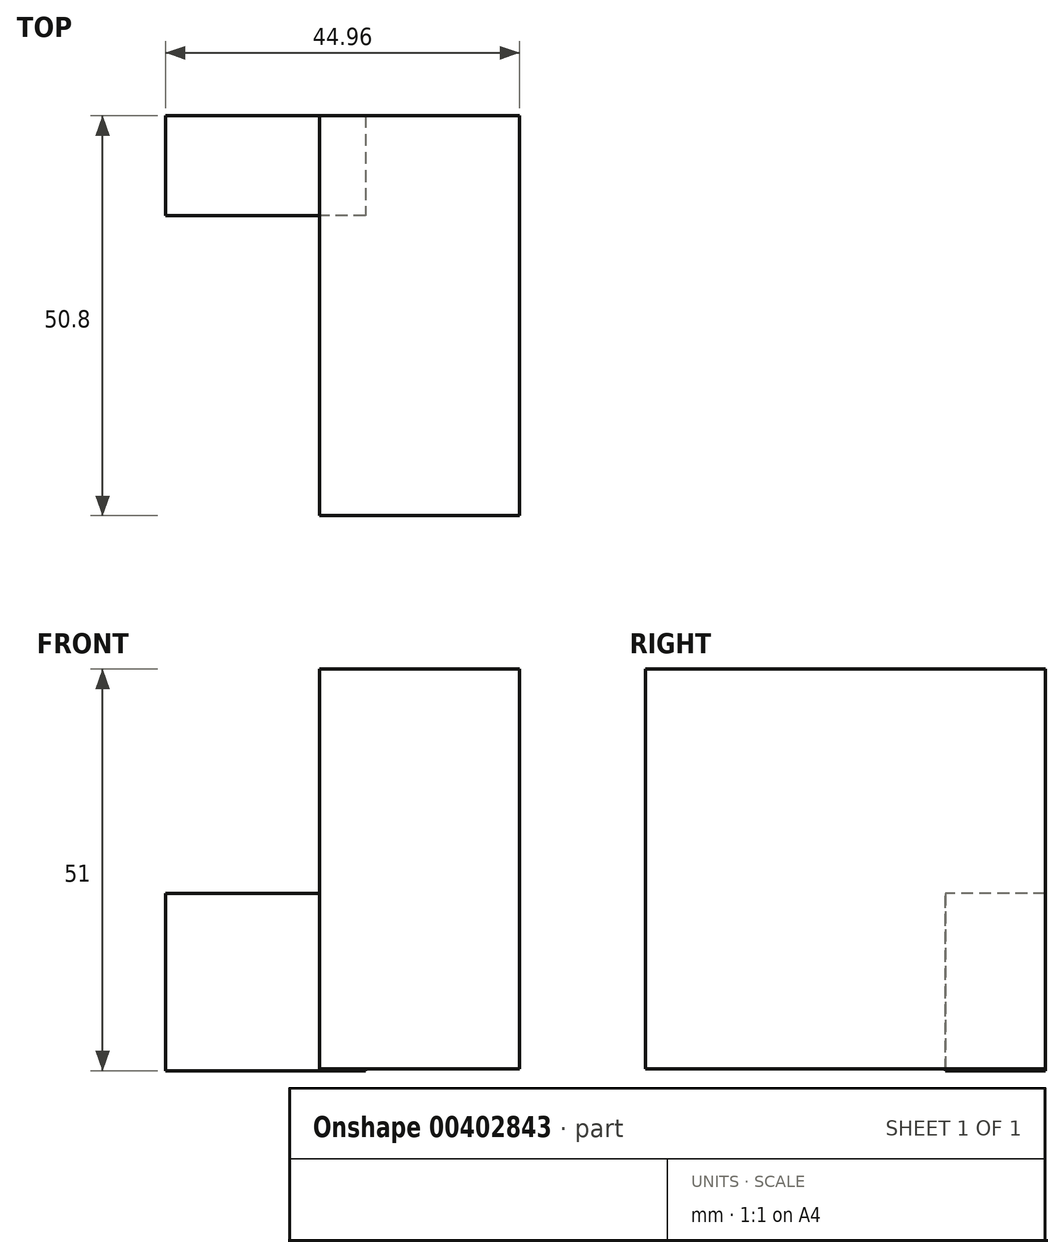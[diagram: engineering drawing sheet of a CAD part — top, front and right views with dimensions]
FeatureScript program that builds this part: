
annotation { "Feature Type Name" : "Feature", "Feature Type Description" : "" }
export const myFeature = defineFeature(function(context is Context, id is Id, definition is map)
    precondition{}
    {
        {
            var Q0;
            Q0=qCreatedBy(makeId("Front.planeOp"),FACE);
            var sketch = newSketch(context, id + "F0", { "sketchPlane" : qUnion([Q0])});
            skLineSegment(sketch, "E0", {"start": v(30.14, -31.41) * mm, "end": v(30.14, 19.39) * mm});
            skLineSegment(sketch, "E1", {"start": v(30.14, 19.39) * mm, "end": v(4.74, 19.39) * mm});
            skLineSegment(sketch, "E2", {"start": v(30.14, -31.41) * mm, "end": v(4.74, -31.41) * mm});
            skLineSegment(sketch, "E3", {"start": v(4.74, 19.39) * mm, "end": v(4.74, -31.41) * mm});
            skSolve(sketch);
        }
        {
            var Q0;
            Q0 = qSketchRegion(id + "F0", true);
            extrude(context, id + "F1", {"entities" : qUnion([Q0]), "depth" : 50.8 * mm});
        }
        {
            var Q0;
            Q0=qCreatedBy(makeId("Front.planeOp"),FACE);
            var sketch = newSketch(context, id + "F2", { "sketchPlane" : qUnion([Q0])});
            skLineSegment(sketch, "E4", {"start": v(10.58, -7.7) * mm, "end": v(10.58, -31.6) * mm});
            skLineSegment(sketch, "E5", {"start": v(10.58, -31.6) * mm, "end": v(-14.82, -31.6) * mm});
            skLineSegment(sketch, "E6", {"start": v(-14.82, -31.6) * mm, "end": v(-14.82, -9.09) * mm});
            skLineSegment(sketch, "E7", {"start": v(-14.82, -9.09) * mm, "end": v(4.54, -9.09) * mm});
            skLineSegment(sketch, "E8", {"start": v(4.54, -9.09) * mm, "end": v(10.58, -9.09) * mm});
            skSolve(sketch);
        }
        {
            var Q0;
            Q0 = qSketchRegion(id + "F2", true);
            extrude(context, id + "F3", {"entities" : qUnion([Q0]), "operationType" : NewBodyOperationType.ADD, "depth" : 12.7 * mm});
        }
    });
